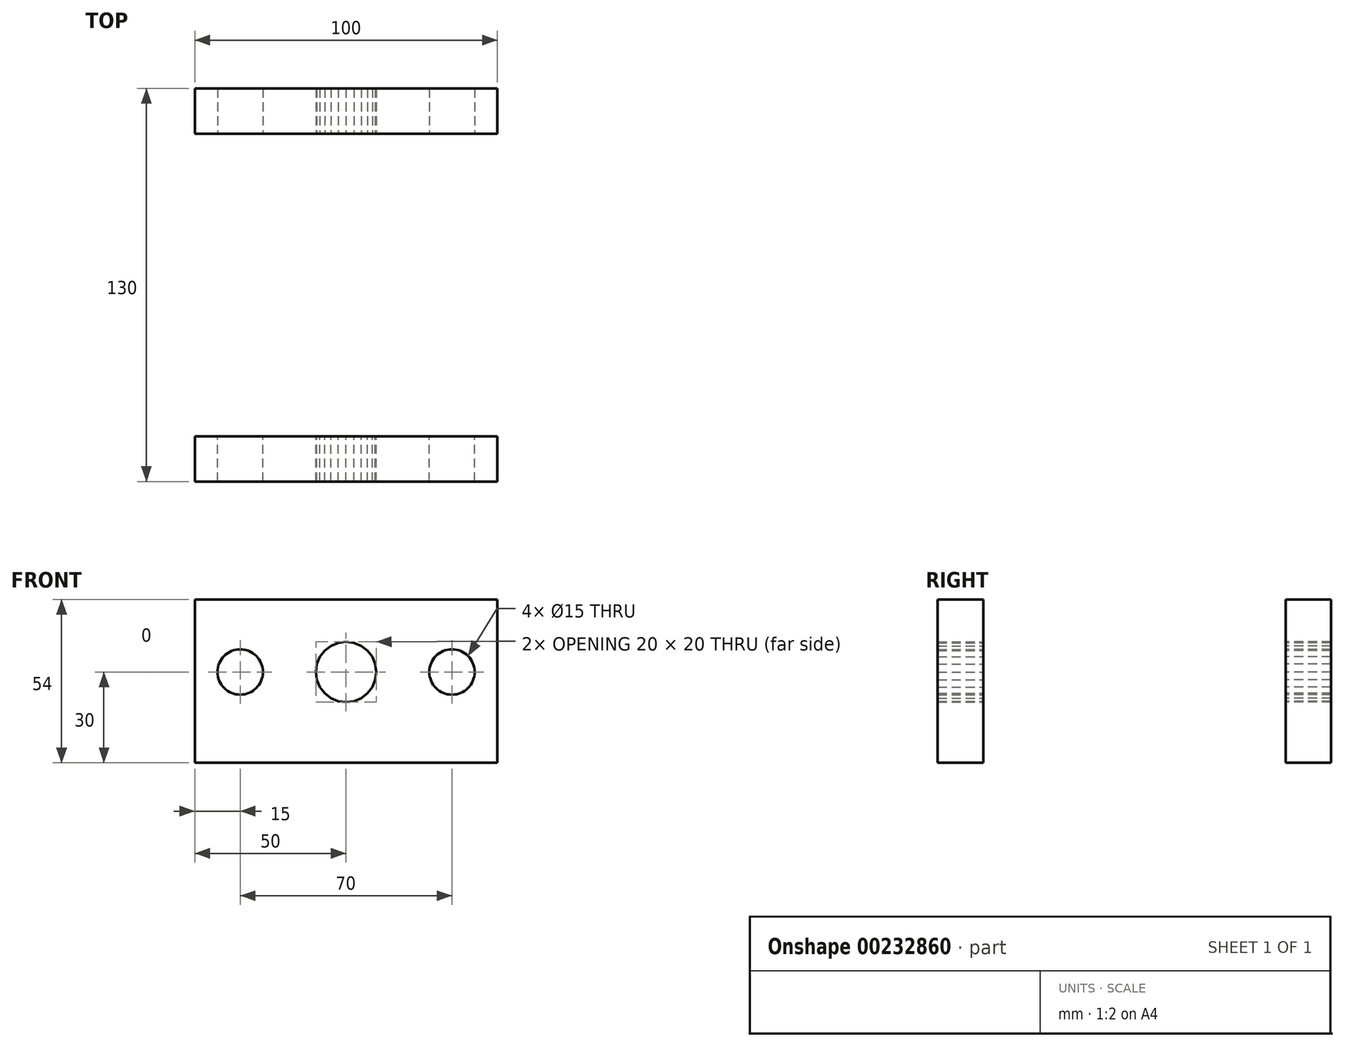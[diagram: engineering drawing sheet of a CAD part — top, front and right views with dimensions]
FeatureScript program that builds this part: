
annotation { "Feature Type Name" : "Feature", "Feature Type Description" : "" }
export const myFeature = defineFeature(function(context is Context, id is Id, definition is map)
    precondition{}
    {
        {
            var Q0;
            Q0=qCreatedBy(makeId("Front.planeOp"),FACE);
            var sketch = newSketch(context, id + "F0", { "sketchPlane" : qUnion([Q0])});
            skLineSegment(sketch, "E0", {"start": v(50, 27) * mm, "end": v(50, -27) * mm});
            skLineSegment(sketch, "E1", {"start": v(50, -27) * mm, "end": v(-50, -27) * mm});
            skLineSegment(sketch, "E2", {"start": v(-50, -27) * mm, "end": v(-50, 27) * mm});
            skLineSegment(sketch, "E3", {"start": v(-50, 27) * mm, "end": v(50, 27) * mm});
            skLineSegment(sketch, "E4", {"start": v(-2.59, 12.66) * mm, "end": v(-5, 11.66) * mm});
            skLineSegment(sketch, "E5", {"start": v(-5, 11.66) * mm, "end": v(-7.07, 10.07) * mm});
            skLineSegment(sketch, "E6", {"start": v(-7.07, 10.07) * mm, "end": v(-8.66, 8) * mm});
            skLineSegment(sketch, "E7", {"start": v(-8.66, 8) * mm, "end": v(-9.66, 5.59) * mm});
            skLineSegment(sketch, "E8", {"start": v(-9.66, 5.59) * mm, "end": v(-10, 3) * mm});
            skLineSegment(sketch, "E9", {"start": v(-10, 3) * mm, "end": v(-9.66, 0.41) * mm});
            skLineSegment(sketch, "E10", {"start": v(-9.66, 0.41) * mm, "end": v(-8.66, -2) * mm});
            skLineSegment(sketch, "E11", {"start": v(-8.66, -2) * mm, "end": v(-7.07, -4.07) * mm});
            skLineSegment(sketch, "E12", {"start": v(-7.07, -4.07) * mm, "end": v(-5, -5.66) * mm});
            skLineSegment(sketch, "E13", {"start": v(-5, -5.66) * mm, "end": v(-2.59, -6.66) * mm});
            skLineSegment(sketch, "E14", {"start": v(-2.59, -6.66) * mm, "end": v(0, -7) * mm});
            skLineSegment(sketch, "E15", {"start": v(0, -7) * mm, "end": v(2.59, -6.66) * mm});
            skLineSegment(sketch, "E16", {"start": v(2.59, -6.66) * mm, "end": v(5, -5.66) * mm});
            skLineSegment(sketch, "E17", {"start": v(5, -5.66) * mm, "end": v(7.07, -4.07) * mm});
            skLineSegment(sketch, "E18", {"start": v(7.07, -4.07) * mm, "end": v(8.66, -2) * mm});
            skLineSegment(sketch, "E19", {"start": v(8.66, -2) * mm, "end": v(9.66, 0.41) * mm});
            skLineSegment(sketch, "E20", {"start": v(9.66, 0.41) * mm, "end": v(10, 3) * mm});
            skLineSegment(sketch, "E21", {"start": v(10, 3) * mm, "end": v(9.66, 5.59) * mm});
            skLineSegment(sketch, "E22", {"start": v(9.66, 5.59) * mm, "end": v(8.66, 8) * mm});
            skLineSegment(sketch, "E23", {"start": v(8.66, 8) * mm, "end": v(7.07, 10.07) * mm});
            skLineSegment(sketch, "E24", {"start": v(7.07, 10.07) * mm, "end": v(5, 11.66) * mm});
            skLineSegment(sketch, "E25", {"start": v(5, 11.66) * mm, "end": v(2.59, 12.66) * mm});
            skLineSegment(sketch, "E26", {"start": v(2.59, 12.66) * mm, "end": v(0, 13) * mm});
            skLineSegment(sketch, "E27", {"start": v(0, 13) * mm, "end": v(-2.59, 12.66) * mm});
            skCircle(sketch, "E28", {"center": v(-35, 3) * mm, "radius": 7.5 * mm});
            skCircle(sketch, "E29", {"center": v(35, 3) * mm, "radius": 7.5 * mm});
            skSolve(sketch);
        }
        {
            var Q0;
            Q0=makeQuery(id+"F0.imprint","IMPRINT",FACE,{"disambiguationData":[TD([[makeQuery(id+"F0.imprint","IMPRINT",EDGE,{"derivedFrom":sQuery(id+"F0.wireOp",EDGE,"E0")}),-1.0]])]});
            cPlane(context, id + "F1", {"entities" : qUnion([Q0]), "cplaneType" : CPlaneType.OFFSET, "offset" : 50 * mm, "width" : 150 * mm, "height" : 150 * mm});
        }
        {
            var Q0;
            Q0=makeQuery(id+"F0.imprint","IMPRINT",FACE,{"disambiguationData":[TD([[makeQuery(id+"F0.imprint","IMPRINT",EDGE,{"derivedFrom":sQuery(id+"F0.wireOp",EDGE,"E0")}),-1.0]])]});
            extrude(context, id + "F2", {"entities" : qUnion([Q0]), "oppositeDirection" : true, "depth" : 15 * mm});
        }
        {
            var Q0;
            Q0=makeQuery(id+"F2.opExtrude","SWEPT_BODY",BODY,{"disambiguationData":[OSD([sQuery(id+"F0.wireOp",EDGE,"E0"),sQuery(id+"F0.wireOp",EDGE,"E1"),sQuery(id+"F0.wireOp",EDGE,"E2"),sQuery(id+"F0.wireOp",EDGE,"E3"),sQuery(id+"F0.wireOp",EDGE,"E4"),sQuery(id+"F0.wireOp",EDGE,"E5"),sQuery(id+"F0.wireOp",EDGE,"E6"),sQuery(id+"F0.wireOp",EDGE,"E7"),sQuery(id+"F0.wireOp",EDGE,"E8"),sQuery(id+"F0.wireOp",EDGE,"E9"),sQuery(id+"F0.wireOp",EDGE,"E10"),sQuery(id+"F0.wireOp",EDGE,"E11"),sQuery(id+"F0.wireOp",EDGE,"E12"),sQuery(id+"F0.wireOp",EDGE,"E13"),sQuery(id+"F0.wireOp",EDGE,"E14"),sQuery(id+"F0.wireOp",EDGE,"E15"),sQuery(id+"F0.wireOp",EDGE,"E16"),sQuery(id+"F0.wireOp",EDGE,"E17"),sQuery(id+"F0.wireOp",EDGE,"E18"),sQuery(id+"F0.wireOp",EDGE,"E19"),sQuery(id+"F0.wireOp",EDGE,"E20"),sQuery(id+"F0.wireOp",EDGE,"E21"),sQuery(id+"F0.wireOp",EDGE,"E22"),sQuery(id+"F0.wireOp",EDGE,"E23"),sQuery(id+"F0.wireOp",EDGE,"E24"),sQuery(id+"F0.wireOp",EDGE,"E25"),sQuery(id+"F0.wireOp",EDGE,"E26"),sQuery(id+"F0.wireOp",EDGE,"E27"),sQuery(id+"F0.wireOp",EDGE,"E28"),sQuery(id+"F0.wireOp",EDGE,"E29")])]});
            var Q1;
            Q1=qCreatedBy(id+"F1.planeOp",FACE);
            mirror(context, id + "F3", {"entities" : qUnion([Q0]), "mirrorPlane" : qUnion([Q1])});
        }
    });
